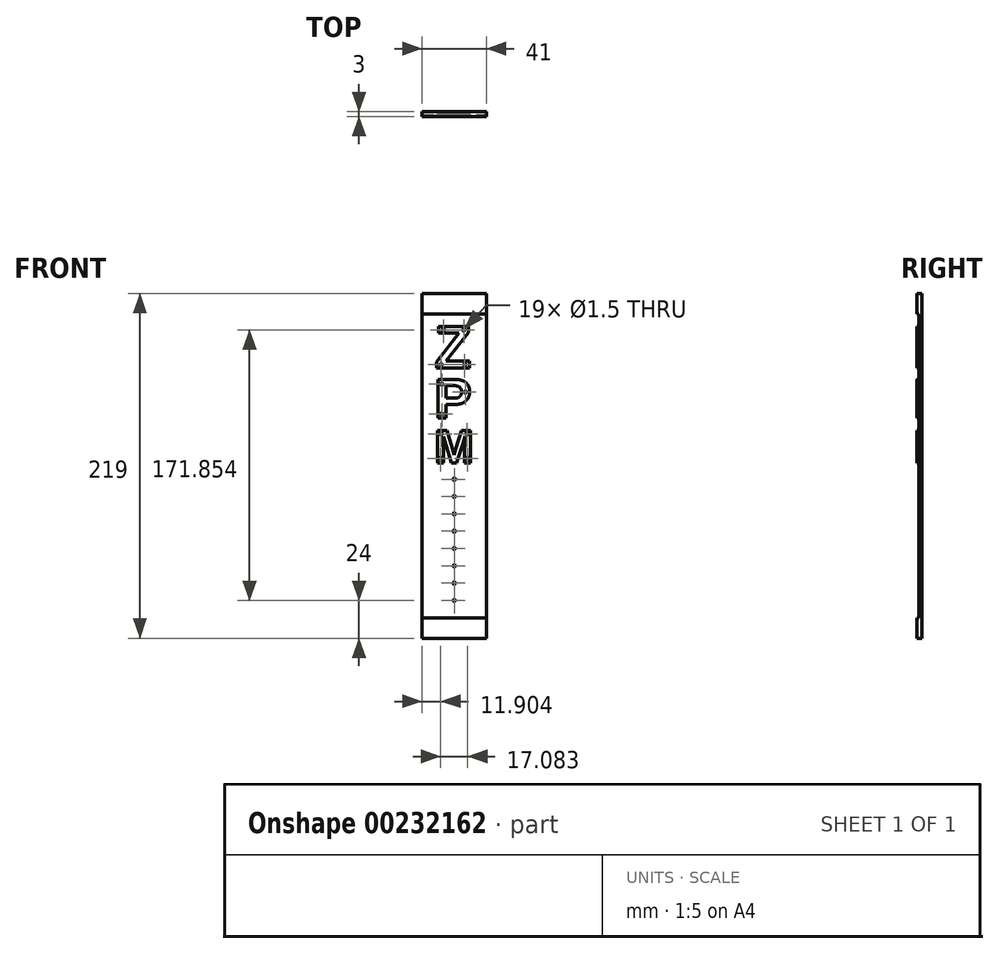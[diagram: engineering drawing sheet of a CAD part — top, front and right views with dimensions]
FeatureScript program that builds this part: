
annotation { "Feature Type Name" : "Feature", "Feature Type Description" : "" }
export const myFeature = defineFeature(function(context is Context, id is Id, definition is map)
    precondition{}
    {
        {
            var Q0;
            Q0=qCreatedBy(makeId("Front.planeOp"),FACE);
            var sketch = newSketch(context, id + "F0", { "sketchPlane" : qUnion([Q0])});
            skLineSegment(sketch, "E0.bottom", {"start": v(-20.5, 109.5) * mm, "end": v(20.5, 109.5) * mm});
            skLineSegment(sketch, "E0.top", {"start": v(-20.5, -109.5) * mm, "end": v(20.5, -109.5) * mm});
            skLineSegment(sketch, "E0.left", {"start": v(-20.5, 109.5) * mm, "end": v(-20.5, -109.5) * mm});
            skLineSegment(sketch, "E0.right", {"start": v(20.5, 109.5) * mm, "end": v(20.5, -109.5) * mm});
            skPoint(sketch, "E0.middle", {"position": v(0, 0) * mm});
            skSolve(sketch);
        }
        {
            var Q0;
            Q0 = qSketchRegion(id + "F0", true);
            extrude(context, id + "F1", {"entities" : qUnion([Q0]), "depth" : 2 * mm});
        }
        {
            var Q0;
            Q0=makeQuery(id+"F1.opExtrude","CAP_FACE",FACE,{"disambiguationData":[OSD([sQuery(id+"F0.wireOp",EDGE,"E0.bottom"),sQuery(id+"F0.wireOp",EDGE,"E0.top"),sQuery(id+"F0.wireOp",EDGE,"E0.left"),sQuery(id+"F0.wireOp",EDGE,"E0.right")])],"isStart":false});
            var sketch = newSketch(context, id + "F2", { "sketchPlane" : qUnion([Q0])});
            skLineSegment(sketch, "E1.bottom", {"start": v(-20.5, 109.5) * mm, "end": v(20.5, 109.5) * mm});
            skLineSegment(sketch, "E1.top", {"start": v(-20.5, 96.5) * mm, "end": v(20.5, 96.5) * mm});
            skLineSegment(sketch, "E1.left", {"start": v(-20.5, 109.5) * mm, "end": v(-20.5, 96.5) * mm});
            skLineSegment(sketch, "E1.right", {"start": v(20.5, 109.5) * mm, "end": v(20.5, 96.5) * mm});
            skLineSegment(sketch, "E2.bottom", {"start": v(-20.5, -109.5) * mm, "end": v(20.5, -109.5) * mm});
            skLineSegment(sketch, "E2.top", {"start": v(-20.5, -96.5) * mm, "end": v(20.5, -96.5) * mm});
            skLineSegment(sketch, "E2.left", {"start": v(-20.5, -109.5) * mm, "end": v(-20.5, -96.5) * mm});
            skLineSegment(sketch, "E2.right", {"start": v(20.5, -109.5) * mm, "end": v(20.5, -96.5) * mm});
            skSolve(sketch);
        }
        {
            var Q0;
            Q0 = qSketchRegion(id + "F2", true);
            extrude(context, id + "F3", {"entities" : qUnion([Q0]), "operationType" : NewBodyOperationType.ADD, "depth" : 1 * mm});
        }
        {
            var Q0;
            Q0=makeQuery(id+"F1.opExtrude","CAP_FACE",FACE,{"disambiguationData":[OSD([sQuery(id+"F0.wireOp",EDGE,"E0.bottom"),sQuery(id+"F0.wireOp",EDGE,"E0.top"),sQuery(id+"F0.wireOp",EDGE,"E0.left"),sQuery(id+"F0.wireOp",EDGE,"E0.right")])],"isStart":false});
            var sketch = newSketch(context, id + "F4", { "sketchPlane" : qUnion([Q0])});
            skText(sketch, "E3", { "text": "Z", "fontName": "Arimo-Bold.ttf"});
            const initialGuessF4  = {"E3": [-0.0125, 0.0622, 1, 0, 0.02763]};
            skSetInitialGuess(sketch, initialGuessF4);
            skSolve(sketch);
        }
        {
            var Q0;
            Q0 = qSketchRegion(id + "F4", true);
            extrude(context, id + "F5", {"entities" : qUnion([Q0]), "operationType" : NewBodyOperationType.ADD, "depth" : 1 * mm});
        }
        {
            var Q0;
            Q0=makeQuery(id+"F5.opExtrude","CAP_FACE",FACE,{"disambiguationData":[OSD([sQuery(id+"F4.wireOp",EDGE,"E3.sketch_text.stroke-0"),sQuery(id+"F4.wireOp",EDGE,"E3.sketch_text.stroke-1"),sQuery(id+"F4.wireOp",EDGE,"E3.sketch_text.stroke-2"),sQuery(id+"F4.wireOp",EDGE,"E3.sketch_text.stroke-3"),sQuery(id+"F4.wireOp",EDGE,"E3.sketch_text.stroke-4"),sQuery(id+"F4.wireOp",EDGE,"E3.sketch_text.stroke-5"),sQuery(id+"F4.wireOp",EDGE,"E3.sketch_text.stroke-6"),sQuery(id+"F4.wireOp",EDGE,"E3.sketch_text.stroke-7"),sQuery(id+"F4.wireOp",EDGE,"E3.sketch_text.stroke-8"),sQuery(id+"F4.wireOp",EDGE,"E3.sketch_text.stroke-9")])],"isStart":false});
            var sketch = newSketch(context, id + "F6", { "sketchPlane" : qUnion([Q0])});
            skCircle(sketch, "E4", {"center": v(-6.93, 86.35) * mm, "radius": 1.5 * mm});
            skPoint(sketch, "E4.centerSnap0", {"position": v(-9.93, 86.44) * mm});
            skCircle(sketch, "E5", {"center": v(6.07, 86.35) * mm, "radius": 1.5 * mm});
            skCircle(sketch, "E6", {"center": v(-8.35, 64.35) * mm, "radius": 1.5 * mm});
            skCircle(sketch, "E7", {"center": v(6.65, 64.35) * mm, "radius": 1.5 * mm});
            skSolve(sketch);
        }
        {
            var Q0;
            Q0=sQuery(id+"F6.wireOp",VERTEX,"E4.center");
            var Q1;
            Q1=sQuery(id+"F6.wireOp",VERTEX,"E5.center");
            var Q2;
            Q2=sQuery(id+"F6.wireOp",VERTEX,"E6.center");
            var Q3;
            Q3=sQuery(id+"F6.wireOp",VERTEX,"E7.center");
            var Q4;
            Q4=makeQuery(id+"F1.opExtrude","SWEPT_BODY",BODY,{"disambiguationData":[OSD([sQuery(id+"F0.wireOp",EDGE,"E0.bottom"),sQuery(id+"F0.wireOp",EDGE,"E0.top"),sQuery(id+"F0.wireOp",EDGE,"E0.left"),sQuery(id+"F0.wireOp",EDGE,"E0.right")])]});
            hole(context, id + "F7", {"style" : HoleStyle.SIMPLE, "endStyle" : HoleEndStyle.BLIND, "standardTappedOrClearance" : lookupTablePath({ "standard" : "ISO", "size" : "1.5", "type" : "Drilled" }), "standardBlindInLast" : lookupTablePath({ "standard" : "ISO", "size" : "1.5", "type" : "Drilled" }), "holeDiameter" : 1.5 * mm, "holeDepth" : 4 * mm, "tappedDepth" : 47 * mm, "tapClearance" : 3, "startFromSketch" : true, "locations" : qUnion([Q0, Q1, Q2, Q3]), "scope" : qUnion([Q4])});
        }
        {
            var Q0;
            Q0=makeQuery(id+"F1.opExtrude","CAP_FACE",FACE,{"disambiguationData":[OSD([sQuery(id+"F0.wireOp",EDGE,"E0.bottom"),sQuery(id+"F0.wireOp",EDGE,"E0.top"),sQuery(id+"F0.wireOp",EDGE,"E0.left"),sQuery(id+"F0.wireOp",EDGE,"E0.right")])],"isStart":false});
            var sketch = newSketch(context, id + "F8", { "sketchPlane" : qUnion([Q0])});
            skText(sketch, "E8", { "text": "P", "fontName": "Arimo-Bold.ttf"});
            const initialGuessF8  = {"E8": [-0.01273, 0.0304, 1, 0, 0.02563]};
            skSetInitialGuess(sketch, initialGuessF8);
            skSolve(sketch);
        }
        {
            var Q0;
            Q0 = qSketchRegion(id + "F8", true);
            extrude(context, id + "F9", {"entities" : qUnion([Q0]), "operationType" : NewBodyOperationType.ADD, "depth" : 1 * mm});
        }
        {
            var Q0;
            Q0=makeQuery(id+"F9.opExtrude","CAP_FACE",FACE,{"disambiguationData":[OSD([sQuery(id+"F8.wireOp",EDGE,"E8.sketch_text.stroke-0"),sQuery(id+"F8.wireOp",EDGE,"E8.sketch_text.stroke-1"),sQuery(id+"F8.wireOp",EDGE,"E8.sketch_text.stroke-2"),sQuery(id+"F8.wireOp",EDGE,"E8.sketch_text.stroke-3"),sQuery(id+"F8.wireOp",EDGE,"E8.sketch_text.stroke-4"),sQuery(id+"F8.wireOp",EDGE,"E8.sketch_text.stroke-5"),sQuery(id+"F8.wireOp",EDGE,"E8.sketch_text.stroke-6"),sQuery(id+"F8.wireOp",EDGE,"E8.sketch_text.stroke-7"),sQuery(id+"F8.wireOp",EDGE,"E8.sketch_text.stroke-8"),sQuery(id+"F8.wireOp",EDGE,"E8.sketch_text.stroke-9"),sQuery(id+"F8.wireOp",EDGE,"E8.sketch_text.stroke-10"),sQuery(id+"F8.wireOp",EDGE,"E8.sketch_text.stroke-11"),sQuery(id+"F8.wireOp",EDGE,"E8.sketch_text.stroke-12"),sQuery(id+"F8.wireOp",EDGE,"E8.sketch_text.stroke-13"),sQuery(id+"F8.wireOp",EDGE,"E8.sketch_text.stroke-14"),sQuery(id+"F8.wireOp",EDGE,"E8.sketch_text.stroke-15")])],"isStart":false});
            var sketch = newSketch(context, id + "F10", { "sketchPlane" : qUnion([Q0])});
            skCircle(sketch, "E9", {"center": v(-7.85, 51.89) * mm, "radius": 1.5 * mm});
            skCircle(sketch, "E10", {"center": v(-7.85, 32.89) * mm, "radius": 1.5 * mm});
            skCircle(sketch, "E11", {"center": v(7.15, 46.89) * mm, "radius": 1.5 * mm});
            skSolve(sketch);
        }
        {
            var Q0;
            Q0=sQuery(id+"F10.wireOp",VERTEX,"E9.center");
            var Q1;
            Q1=sQuery(id+"F10.wireOp",VERTEX,"E11.center");
            var Q2;
            Q2=sQuery(id+"F10.wireOp",VERTEX,"E10.center");
            var Q3;
            Q3=makeQuery(id+"F1.opExtrude","SWEPT_BODY",BODY,{"disambiguationData":[OSD([sQuery(id+"F0.wireOp",EDGE,"E0.bottom"),sQuery(id+"F0.wireOp",EDGE,"E0.top"),sQuery(id+"F0.wireOp",EDGE,"E0.left"),sQuery(id+"F0.wireOp",EDGE,"E0.right")])]});
            hole(context, id + "F11", {"style" : HoleStyle.SIMPLE, "endStyle" : HoleEndStyle.BLIND, "standardTappedOrClearance" : lookupTablePath({ "standard" : "ISO", "size" : "1.5", "type" : "Drilled" }), "standardBlindInLast" : lookupTablePath({ "standard" : "ISO", "size" : "1.5", "type" : "Drilled" }), "holeDiameter" : 1.5 * mm, "holeDepth" : 4 * mm, "tappedDepth" : 47 * mm, "tapClearance" : 3, "startFromSketch" : true, "locations" : qUnion([Q0, Q1, Q2]), "scope" : qUnion([Q3])});
        }
        {
            var Q0;
            {var subQ0=sQuery(id+"F0.wireOp",EDGE,"E0.right");var subQ1=sQuery(id+"F0.wireOp",EDGE,"E0.left");Q0=makeQuery(id+"F9.boolean.opBoolean","SPLIT",FACE,{"disambiguationData":[TD([makeQuery(id+"F1.opExtrude","SWEPT_FACE",FACE,{"disambiguationData":[OSD([subQ1])]})])],"derivedFrom":makeQuery(id+"F1.opExtrude","CAP_FACE",FACE,{"disambiguationData":[OSD([sQuery(id+"F0.wireOp",EDGE,"E0.bottom"),sQuery(id+"F0.wireOp",EDGE,"E0.top"),subQ1,subQ0])],"isStart":false})});}
            var sketch = newSketch(context, id + "F12", { "sketchPlane" : qUnion([Q0])});
            skText(sketch, "E12", { "text": "M", "fontName": "Arimo-Bold.ttf"});
            const initialGuessF12  = {"E12": [-0.01252, 0.00174, 1, 0, 0.02154]};
            skSetInitialGuess(sketch, initialGuessF12);
            skSolve(sketch);
        }
        {
            var Q0;
            Q0 = qSketchRegion(id + "F12", true);
            extrude(context, id + "F13", {"entities" : qUnion([Q0]), "operationType" : NewBodyOperationType.ADD, "depth" : 1 * mm});
        }
        {
            var Q0;
            Q0=makeQuery(id+"F13.opExtrude","CAP_FACE",FACE,{"disambiguationData":[OSD([sQuery(id+"F12.wireOp",EDGE,"E12.sketch_text.stroke-0"),sQuery(id+"F12.wireOp",EDGE,"E12.sketch_text.stroke-1"),sQuery(id+"F12.wireOp",EDGE,"E12.sketch_text.stroke-2"),sQuery(id+"F12.wireOp",EDGE,"E12.sketch_text.stroke-3"),sQuery(id+"F12.wireOp",EDGE,"E12.sketch_text.stroke-4"),sQuery(id+"F12.wireOp",EDGE,"E12.sketch_text.stroke-5"),sQuery(id+"F12.wireOp",EDGE,"E12.sketch_text.stroke-6"),sQuery(id+"F12.wireOp",EDGE,"E12.sketch_text.stroke-7"),sQuery(id+"F12.wireOp",EDGE,"E12.sketch_text.stroke-8"),sQuery(id+"F12.wireOp",EDGE,"E12.sketch_text.stroke-9"),sQuery(id+"F12.wireOp",EDGE,"E12.sketch_text.stroke-10"),sQuery(id+"F12.wireOp",EDGE,"E12.sketch_text.stroke-11"),sQuery(id+"F12.wireOp",EDGE,"E12.sketch_text.stroke-12"),sQuery(id+"F12.wireOp",EDGE,"E12.sketch_text.stroke-13"),sQuery(id+"F12.wireOp",EDGE,"E12.sketch_text.stroke-14"),sQuery(id+"F12.wireOp",EDGE,"E12.sketch_text.stroke-15"),sQuery(id+"F12.wireOp",EDGE,"E12.sketch_text.stroke-16"),sQuery(id+"F12.wireOp",EDGE,"E12.sketch_text.stroke-17"),sQuery(id+"F12.wireOp",EDGE,"E12.sketch_text.stroke-18"),sQuery(id+"F12.wireOp",EDGE,"E12.sketch_text.stroke-19"),sQuery(id+"F12.wireOp",EDGE,"E12.sketch_text.stroke-20")])],"isStart":false});
            var sketch = newSketch(context, id + "F14", { "sketchPlane" : qUnion([Q0])});
            skCircle(sketch, "E13", {"center": v(-8.27, 20.33) * mm, "radius": 1.5 * mm});
            skCircle(sketch, "E14", {"center": v(8.16, 20.33) * mm, "radius": 1.5 * mm});
            skCircle(sketch, "E15", {"center": v(8.49, 4.74) * mm, "radius": 1.5 * mm});
            skCircle(sketch, "E16", {"center": v(-8.6, 4.74) * mm, "radius": 1.5 * mm});
            skSolve(sketch);
        }
        {
            var Q0;
            Q0=sQuery(id+"F14.wireOp",VERTEX,"E14.center");
            var Q1;
            Q1=sQuery(id+"F14.wireOp",VERTEX,"E15.center");
            var Q2;
            Q2=sQuery(id+"F14.wireOp",VERTEX,"E16.center");
            var Q3;
            Q3=sQuery(id+"F14.wireOp",VERTEX,"E13.center");
            var Q4;
            Q4=makeQuery(id+"F1.opExtrude","SWEPT_BODY",BODY,{"disambiguationData":[OSD([sQuery(id+"F0.wireOp",EDGE,"E0.bottom"),sQuery(id+"F0.wireOp",EDGE,"E0.top"),sQuery(id+"F0.wireOp",EDGE,"E0.left"),sQuery(id+"F0.wireOp",EDGE,"E0.right")])]});
            hole(context, id + "F15", {"style" : HoleStyle.SIMPLE, "endStyle" : HoleEndStyle.BLIND, "standardTappedOrClearance" : lookupTablePath({ "standard" : "ISO", "size" : "1.5", "type" : "Drilled" }), "standardBlindInLast" : lookupTablePath({ "standard" : "ISO", "size" : "1.5", "type" : "Drilled" }), "holeDiameter" : 1.5 * mm, "holeDepth" : 4 * mm, "tappedDepth" : 47 * mm, "tapClearance" : 3, "startFromSketch" : true, "locations" : qUnion([Q0, Q1, Q2, Q3]), "scope" : qUnion([Q4])});
        }
        {
            var Q0;
            {var subQ0=sQuery(id+"F0.wireOp",EDGE,"E0.right");var subQ1=sQuery(id+"F0.wireOp",EDGE,"E0.left");Q0=makeQuery(id+"F9.boolean.opBoolean","SPLIT",FACE,{"disambiguationData":[TD([makeQuery(id+"F1.opExtrude","SWEPT_FACE",FACE,{"disambiguationData":[OSD([subQ1])]})])],"derivedFrom":makeQuery(id+"F1.opExtrude","CAP_FACE",FACE,{"disambiguationData":[OSD([sQuery(id+"F0.wireOp",EDGE,"E0.bottom"),sQuery(id+"F0.wireOp",EDGE,"E0.top"),subQ1,subQ0])],"isStart":false})});}
            var sketch = newSketch(context, id + "F16", { "sketchPlane" : qUnion([Q0])});
            skLineSegment(sketch, "E17", {"start": v(0, 0) * mm, "end": v(0, -96.5) * mm});
            skCircle(sketch, "E18", {"center": v(0, -8.5) * mm, "radius": 4 * mm});
            skCircle(sketch, "E19", {"center": v(0, -19.5) * mm, "radius": 4 * mm});
            skCircle(sketch, "E20", {"center": v(0, -30.5) * mm, "radius": 4 * mm});
            skCircle(sketch, "E21", {"center": v(0, -41.5) * mm, "radius": 4 * mm});
            skCircle(sketch, "E22", {"center": v(0, -52.5) * mm, "radius": 4 * mm});
            skCircle(sketch, "E23", {"center": v(0, -63.5) * mm, "radius": 4 * mm});
            skCircle(sketch, "E24", {"center": v(0, -74.5) * mm, "radius": 4 * mm});
            skCircle(sketch, "E25", {"center": v(0, -85.5) * mm, "radius": 4 * mm});
            skSolve(sketch);
        }
        {
            var Q0;
            Q0=sQuery(id+"F16.wireOp",VERTEX,"E18.center");
            var Q1;
            Q1=sQuery(id+"F16.wireOp",VERTEX,"E19.center");
            var Q2;
            Q2=sQuery(id+"F16.wireOp",VERTEX,"E20.center");
            var Q3;
            Q3=sQuery(id+"F16.wireOp",VERTEX,"E21.center");
            var Q4;
            Q4=sQuery(id+"F16.wireOp",VERTEX,"E22.center");
            var Q5;
            Q5=sQuery(id+"F16.wireOp",VERTEX,"E23.center");
            var Q6;
            Q6=sQuery(id+"F16.wireOp",VERTEX,"E24.center");
            var Q7;
            Q7=sQuery(id+"F16.wireOp",VERTEX,"E25.center");
            var Q8;
            Q8=makeQuery(id+"F1.opExtrude","SWEPT_BODY",BODY,{"disambiguationData":[OSD([sQuery(id+"F0.wireOp",EDGE,"E0.bottom"),sQuery(id+"F0.wireOp",EDGE,"E0.top"),sQuery(id+"F0.wireOp",EDGE,"E0.left"),sQuery(id+"F0.wireOp",EDGE,"E0.right")])]});
            hole(context, id + "F17", {"style" : HoleStyle.SIMPLE, "endStyle" : HoleEndStyle.BLIND, "standardTappedOrClearance" : lookupTablePath({ "standard" : "ISO", "size" : "1.5", "type" : "Drilled" }), "standardBlindInLast" : lookupTablePath({ "standard" : "ISO", "size" : "1.5", "type" : "Drilled" }), "holeDiameter" : 1.5 * mm, "holeDepth" : 4 * mm, "tappedDepth" : 47 * mm, "tapClearance" : 3, "startFromSketch" : true, "locations" : qUnion([Q0, Q1, Q2, Q3, Q4, Q5, Q6, Q7]), "scope" : qUnion([Q8])});
        }
    });
